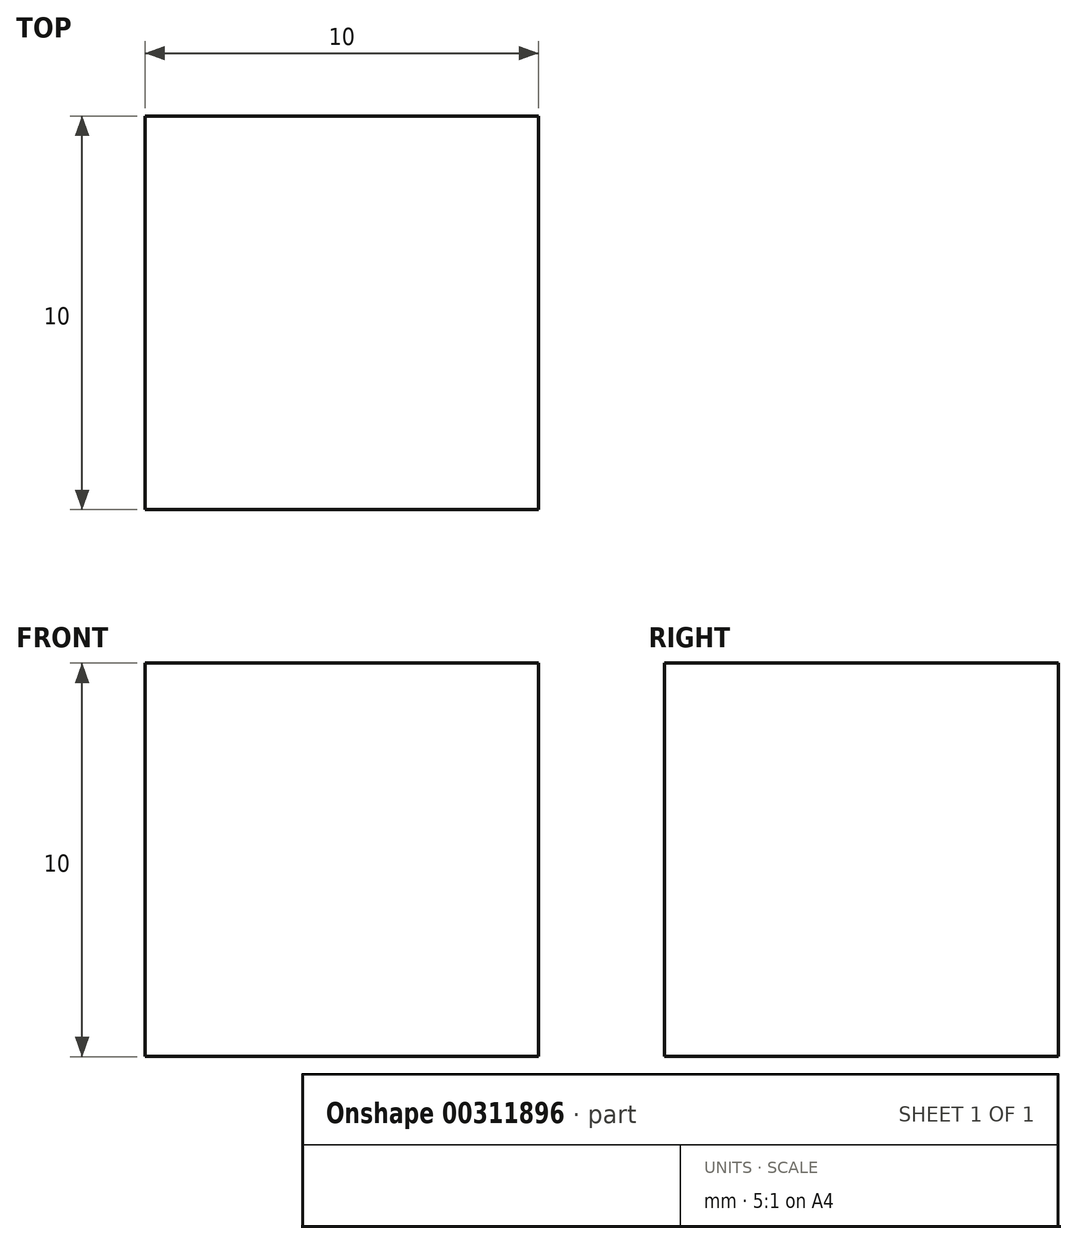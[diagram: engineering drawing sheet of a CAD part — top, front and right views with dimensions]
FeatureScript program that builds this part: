
annotation { "Feature Type Name" : "Feature", "Feature Type Description" : "" }
export const myFeature = defineFeature(function(context is Context, id is Id, definition is map)
    precondition{}
    {
        {
            var Q0;
            Q0=qCreatedBy(makeId("Front.planeOp"),FACE);
            var sketch = newSketch(context, id + "F0", { "sketchPlane" : qUnion([Q0])});
            skLineSegment(sketch, "E0.bottom", {"start": v(-4, 3.87) * mm, "end": v(6, 3.87) * mm});
            skLineSegment(sketch, "E0.top", {"start": v(-4, -6.13) * mm, "end": v(6, -6.13) * mm});
            skLineSegment(sketch, "E0.left", {"start": v(-4, 3.87) * mm, "end": v(-4, -6.13) * mm});
            skLineSegment(sketch, "E0.right", {"start": v(6, 3.87) * mm, "end": v(6, -6.13) * mm});
            skSolve(sketch);
        }
        {
            var Q0;
            Q0 = qSketchRegion(id + "F0", true);
            extrude(context, id + "F1", {"entities" : qUnion([Q0]), "depth" : 10 * mm, "offsetDistance" : 25 * mm});
        }
    });
